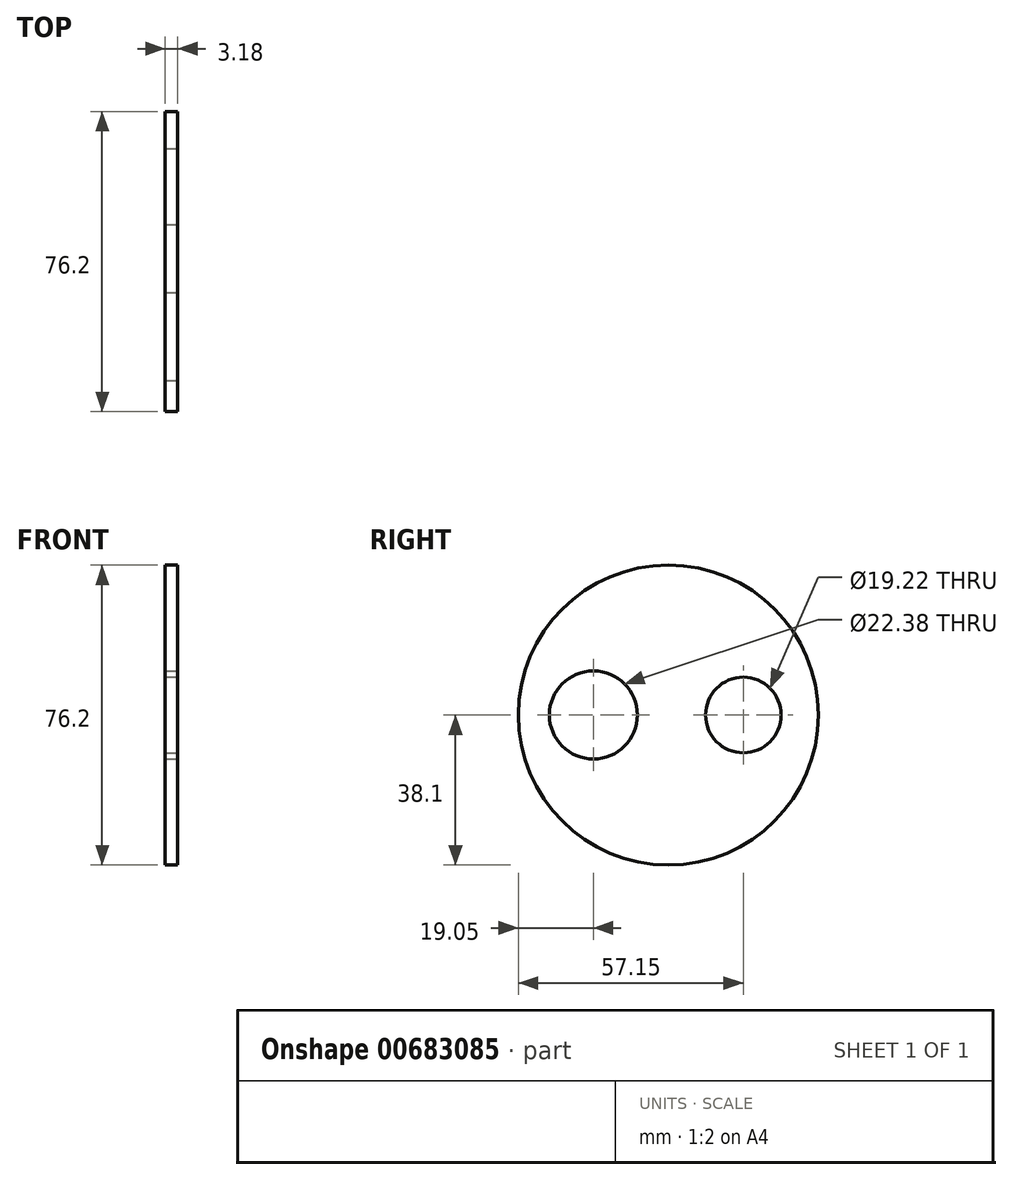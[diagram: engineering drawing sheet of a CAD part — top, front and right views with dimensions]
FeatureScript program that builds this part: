
annotation { "Feature Type Name" : "Feature", "Feature Type Description" : "" }
export const myFeature = defineFeature(function(context is Context, id is Id, definition is map)
    precondition{}
    {
        {
            var Q0;
            Q0=qCreatedBy(makeId("Right.planeOp"),FACE);
            var sketch = newSketch(context, id + "F0", { "sketchPlane" : qUnion([Q0])});
            skCircle(sketch, "E0", {"center": v(0, 0) * mm, "radius": 38.1 * mm});
            skSolve(sketch);
        }
        {
            var Q0;
            Q0 = qSketchRegion(id + "F0", true);
            extrude(context, id + "F1", {"entities" : qUnion([Q0]), "depth" : 3.17 * mm, "offsetDistance" : 25.4 * mm});
        }
        {
            var Q0;
            Q0=makeQuery(id+"F1.opExtrude","CAP_FACE",FACE,{"disambiguationData":[OSD([sQuery(id+"F0.wireOp",EDGE,"E0")])],"isStart":false});
            var sketch = newSketch(context, id + "F2", { "sketchPlane" : qUnion([Q0])});
            skCircle(sketch, "E1", {"center": v(-19.05, 0) * mm, "radius": 11.19 * mm});
            skCircle(sketch, "E2", {"center": v(19.05, 0) * mm, "radius": 9.6 * mm});
            skSolve(sketch);
        }
        {
            var Q0;
            Q0 = qSketchRegion(id + "F2", true);
            extrude(context, id + "F3", {"entities" : qUnion([Q0]), "operationType" : NewBodyOperationType.REMOVE, "oppositeDirection" : true, "depth" : 25.4 * mm, "offsetDistance" : 25.4 * mm});
        }
    });
